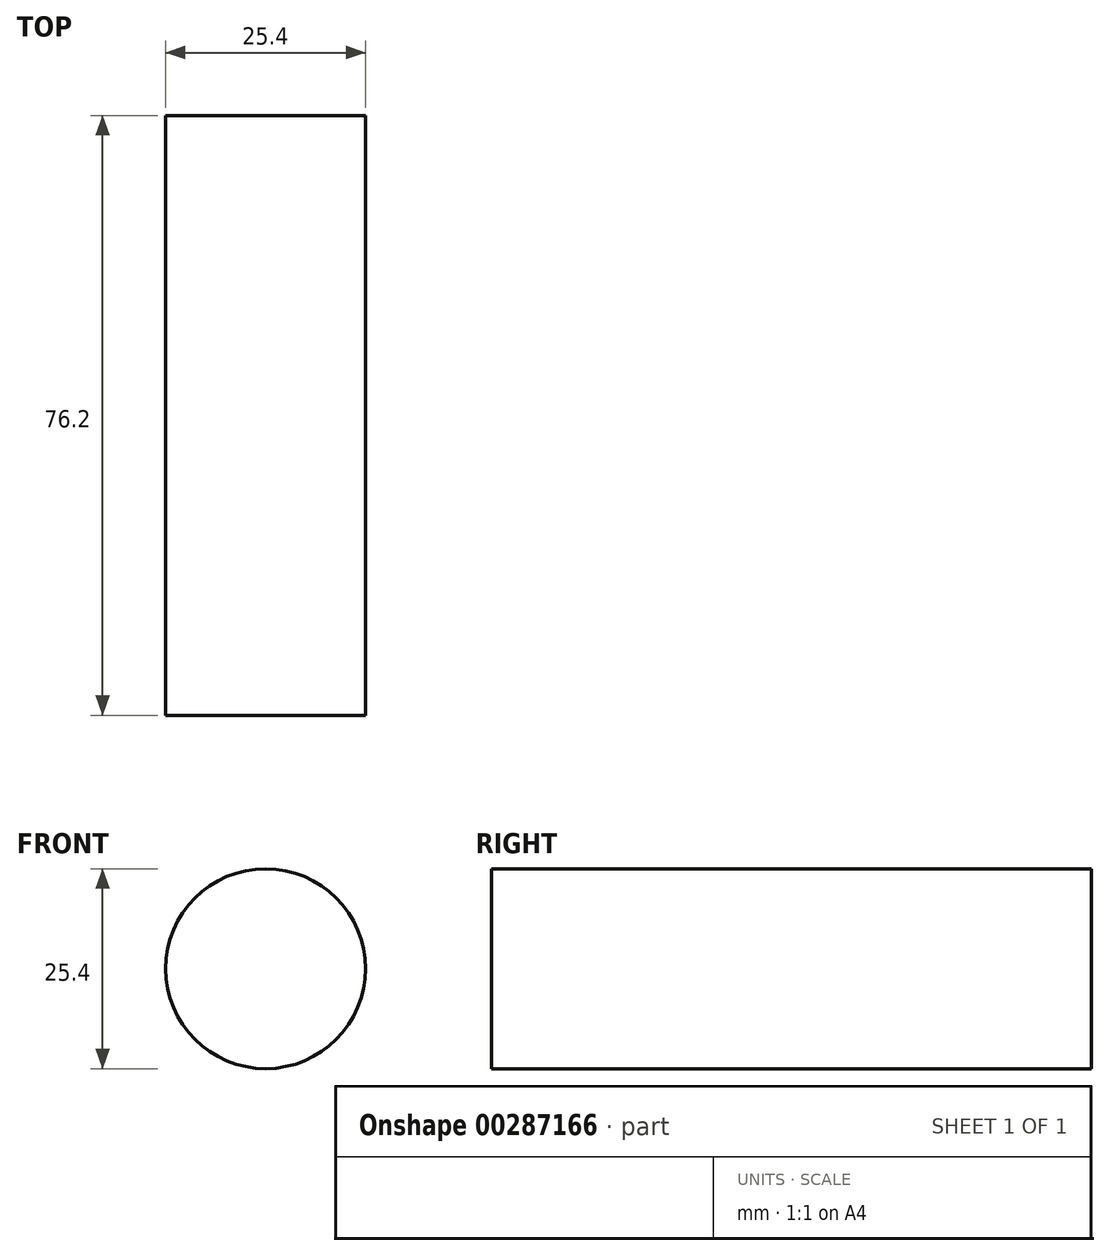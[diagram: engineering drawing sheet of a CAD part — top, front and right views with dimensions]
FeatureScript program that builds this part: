
annotation { "Feature Type Name" : "Feature", "Feature Type Description" : "" }
export const myFeature = defineFeature(function(context is Context, id is Id, definition is map)
    precondition{}
    {
        {
            var Q0;
            Q0=qCreatedBy(makeId("Front.planeOp"),FACE);
            var sketch = newSketch(context, id + "F0", { "sketchPlane" : qUnion([Q0])});
            skCircle(sketch, "E0", {"center": v(-31.5, 38.38) * mm, "radius": 12.7 * mm});
            skSolve(sketch);
        }
        {
            var Q0;
            Q0 = qSketchRegion(id + "F0", true);
            extrude(context, id + "F1", {"entities" : qUnion([Q0]), "depth" : 76.2 * mm});
        }
    });
